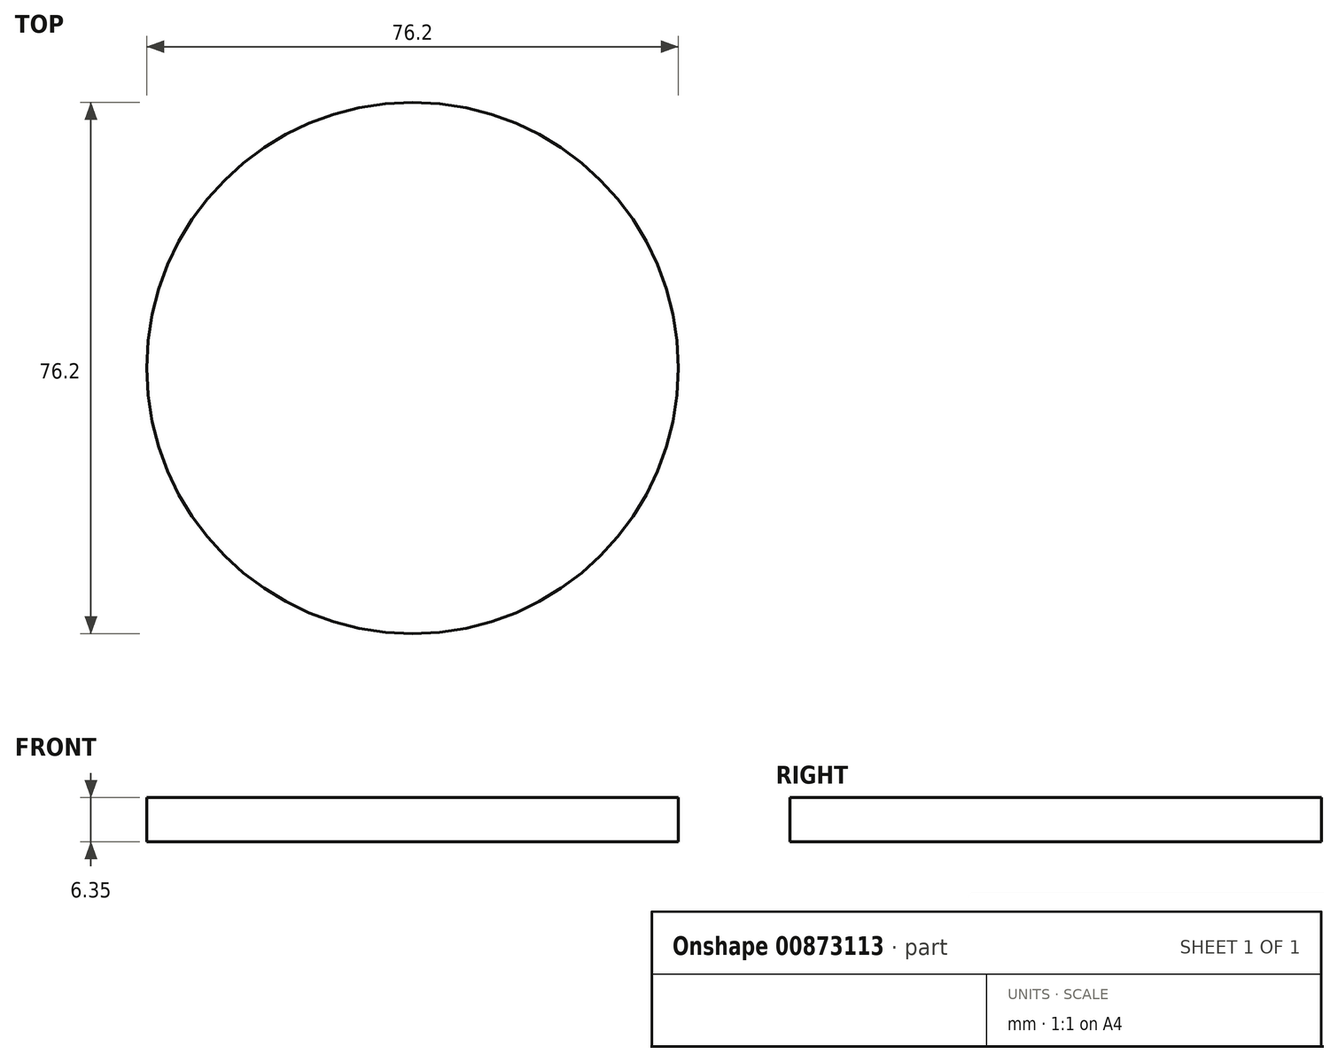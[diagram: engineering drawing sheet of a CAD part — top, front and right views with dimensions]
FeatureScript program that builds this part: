
annotation { "Feature Type Name" : "Feature", "Feature Type Description" : "" }
export const myFeature = defineFeature(function(context is Context, id is Id, definition is map)
    precondition{}
    {
        {
            var Q0;
            Q0=qCreatedBy(makeId("Top.planeOp"),FACE);
            var sketch = newSketch(context, id + "F0", { "sketchPlane" : qUnion([Q0])});
            skCircle(sketch, "E0", {"center": v(0, 0) * mm, "radius": 38.1 * mm});
            skSolve(sketch);
        }
        {
            var Q0;
            Q0 = qSketchRegion(id + "F0", true);
            extrude(context, id + "F1", {"entities" : qUnion([Q0]), "depth" : 6.35 * mm, "offsetDistance" : 25.4 * mm});
        }
    });
